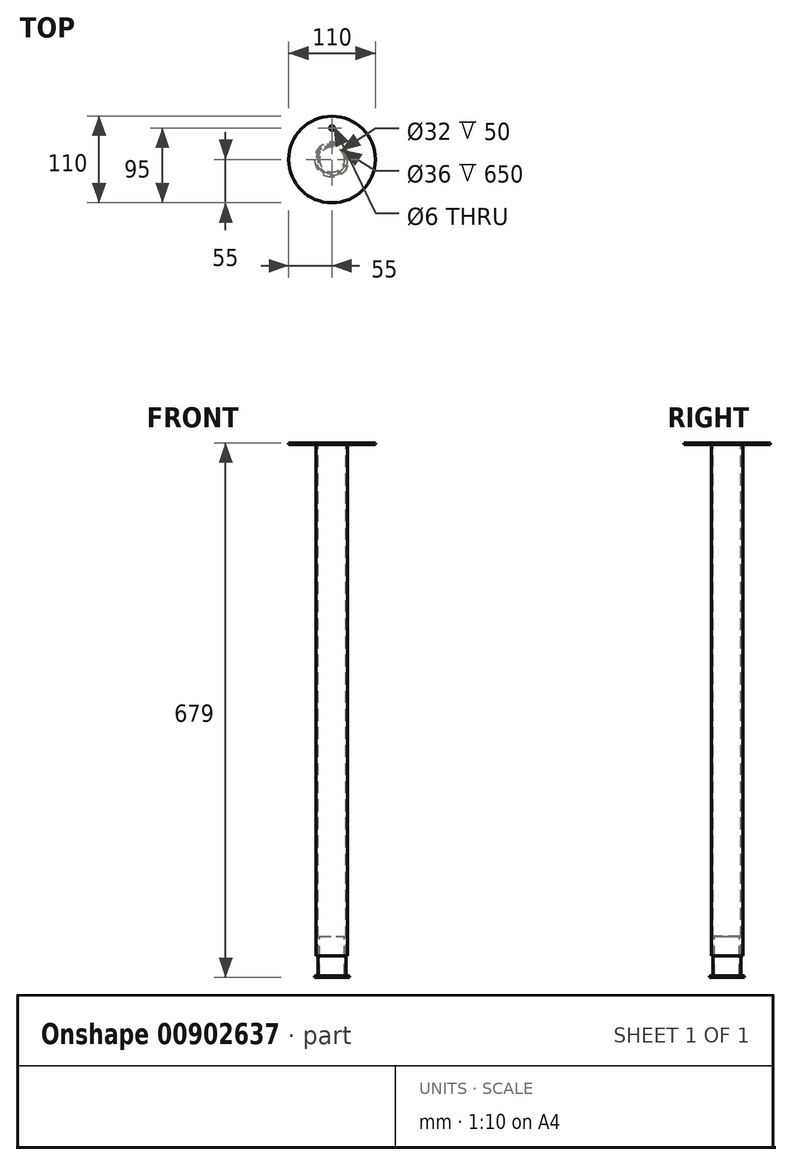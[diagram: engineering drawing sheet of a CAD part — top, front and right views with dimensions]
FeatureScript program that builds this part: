
annotation { "Feature Type Name" : "Feature", "Feature Type Description" : "" }
export const myFeature = defineFeature(function(context is Context, id is Id, definition is map)
    precondition{}
    {
        {
            var Q0;
            Q0=qCreatedBy(makeId("Top.planeOp"),FACE);
            var sketch = newSketch(context, id + "F0", { "sketchPlane" : qUnion([Q0])});
            skCircle(sketch, "E0", {"center": v(0, 0) * mm, "radius": 55 * mm});
            skSolve(sketch);
        }
        {
            var Q0;
            Q0 = qSketchRegion(id + "F0", true);
            extrude(context, id + "F1", {"entities" : qUnion([Q0]), "depth" : 2 * mm, "offsetDistance" : 25 * mm});
        }
        {
            var Q0;
            Q0=makeQuery(id+"F1.opExtrude","CAP_FACE",FACE,{"disambiguationData":[OSD([sQuery(id+"F0.wireOp",EDGE,"E0")])],"isStart":true});
            var sketch = newSketch(context, id + "F2", { "sketchPlane" : qUnion([Q0])});
            skCircle(sketch, "E1", {"center": v(0, 0) * mm, "radius": 20 * mm});
            skCircle(sketch, "E2.0", {"center": v(0, 0) * mm, "radius": 18 * mm});
            skSolve(sketch);
        }
        {
            var Q0;
            Q0 = qSketchRegion(id + "F2", true);
            extrude(context, id + "F3", {"entities" : qUnion([Q0]), "operationType" : NewBodyOperationType.ADD, "depth" : 650 * mm, "offsetDistance" : 25 * mm});
        }
        {
            var Q0;
            Q0=makeQuery(id+"F3.opExtrude","CAP_FACE",FACE,{"disambiguationData":[OSD([sQuery(id+"F2.wireOp",EDGE,"E1"),sQuery(id+"F2.wireOp",EDGE,"E2.0")])],"isStart":false});
            var sketch = newSketch(context, id + "F4", { "sketchPlane" : qUnion([Q0])});
            skCircle(sketch, "E3", {"center": v(0, 0) * mm, "radius": 18 * mm});
            skCircle(sketch, "E4.0", {"center": v(0, 0) * mm, "radius": 16 * mm});
            skSolve(sketch);
        }
        {
            var Q0;
            Q0 = qSketchRegion(id + "F4", true);
            extrude(context, id + "F5", {"entities" : qUnion([Q0]), "depth" : 25 * mm, "offsetDistance" : 25 * mm, "hasSecondDirection" : true, "secondDirectionOppositeDirection" : true, "secondDirectionDepth" : 25 * mm});
        }
        {
            var Q0;
            Q0=makeQuery(id+"F5.opExtrude","CAP_FACE",FACE,{"disambiguationData":[OSD([sQuery(id+"F4.wireOp",EDGE,"E3"),sQuery(id+"F4.wireOp",EDGE,"E4.0")])],"isStart":false});
            var sketch = newSketch(context, id + "F6", { "sketchPlane" : qUnion([Q0])});
            skCircle(sketch, "E5", {"center": v(0, 0) * mm, "radius": 22 * mm});
            skSolve(sketch);
        }
        {
            var Q0;
            Q0 = qSketchRegion(id + "F6", true);
            extrude(context, id + "F7", {"entities" : qUnion([Q0]), "operationType" : NewBodyOperationType.ADD, "depth" : 2 * mm, "offsetDistance" : 25 * mm});
        }
        {
            var Q0;
            {var subQ0=sQuery(id+"F0.wireOp",EDGE,"E0");Q0=makeQuery(id+"F3.boolean.opBoolean","SPLIT",FACE,{"disambiguationData":[TD([makeQuery(id+"F1.opExtrude","SWEPT_FACE",FACE,{"disambiguationData":[OSD([subQ0])]})])],"derivedFrom":makeQuery(id+"F1.opExtrude","CAP_FACE",FACE,{"disambiguationData":[OSD([subQ0])],"isStart":true})});}
            var sketch = newSketch(context, id + "F8", { "sketchPlane" : qUnion([Q0])});
            skCircle(sketch, "E6", {"center": v(0, -40) * mm, "radius": 3 * mm});
            skCircle(sketch, "E7", {"center": v(0, 0) * mm, "radius": 40 * mm, "construction": true});
            skSolve(sketch);
        }
        {
            var Q0;
            Q0 = qSketchRegion(id + "F8", true);
            extrude(context, id + "F9", {"entities" : qUnion([Q0]), "operationType" : NewBodyOperationType.REMOVE, "endBound" : BoundingType.THROUGH_ALL, "oppositeDirection" : true, "depth" : 25 * mm, "offsetDistance" : 25 * mm});
        }
    });
